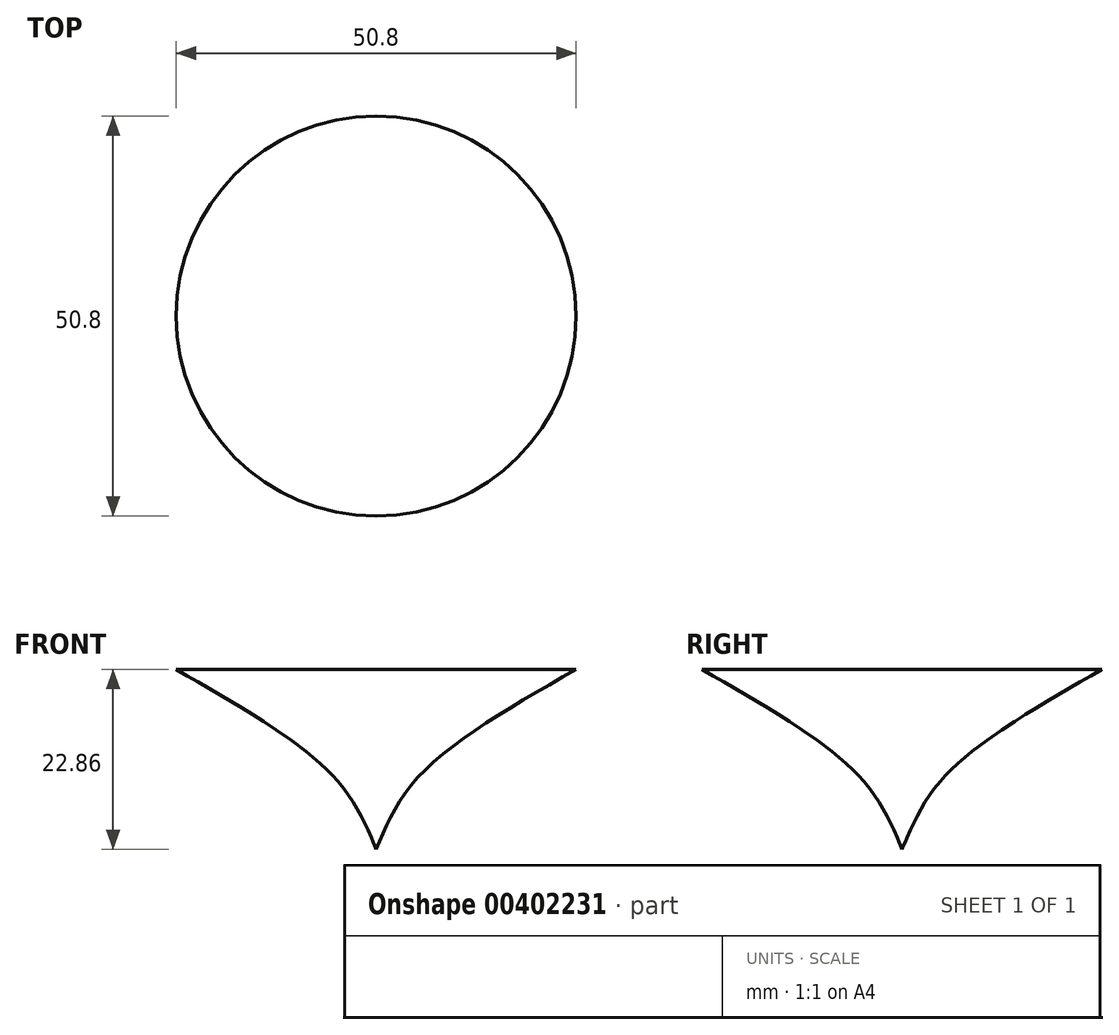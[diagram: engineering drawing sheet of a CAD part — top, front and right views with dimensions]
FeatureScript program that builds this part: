
annotation { "Feature Type Name" : "Feature", "Feature Type Description" : "" }
export const myFeature = defineFeature(function(context is Context, id is Id, definition is map)
    precondition{}
    {
        {
            var Q0;
            Q0=qCreatedBy(makeId("Front.planeOp"),FACE);
            var sketch = newSketch(context, id + "F0", { "sketchPlane" : qUnion([Q0])});
            skLineSegment(sketch, "E0", {"start": v(0, 54.61) * mm, "end": v(0, 31.75) * mm});
            skLineSegment(sketch, "E1", {"start": v(0, 54.61) * mm, "end": v(25.4, 54.61) * mm});
            skFitSpline(sketch, "E2", {"points": [v(25.4, 54.61) * mm, v(5.5, 41.11) * mm, v(0, 31.75) * mm], "startDerivative": vector(-39.13, -22.35) * mm, "endDerivative": vector(-9.75, -23.44) * mm});
            skSolve(sketch);
        }
        {
            var Q0;
            Q0 = qSketchRegion(id + "F0", true);
            var Q1;
            Q1=sQuery(id+"F0.wireOp",EDGE,"E0");
            revolve(context, id + "F1", {"entities" : qUnion([Q0]), "axis" : qUnion([Q1]), "revolveType" : RevolveType.FULL});
        }
    });
